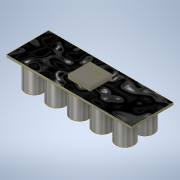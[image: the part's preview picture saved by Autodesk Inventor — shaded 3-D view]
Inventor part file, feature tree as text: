
AUTODESK INVENTOR PART (.ipt)
format: ipt  version: 2020 (Build 240168000, 168)  size: 611,840 bytes
history: native  units: mm
features: chamfer x16, extrude x10, sketch x10, other x2
ambient origin geometry x8: Origin, YZ Plane, XZ Plane, XY Plane, X Axis, Y Axis, Z Axis, Center Point
bodies: Body1 (feature_tree)
feature tree (38):
  other  "Bryła1"
  extrude  "Wyciągnięcie proste1"  Depth=10.0mm
  extrude  "Wyciągnięcie proste2"  Depth=55.88mm
  chamfer  "Faza1"  Distance=27.94mm
  chamfer  "Faza2"  Distance=1.0mm
  chamfer  "Faza3"  Distance=6.03mm
  extrude  "Wyciągnięcie proste3"  Depth=10.0mm
  chamfer  "Faza4"  Distance=2.54mm
  extrude  "Wyciągnięcie proste4"  Depth=10.0mm
  chamfer  "Faza5"  Distance=5.08mm
  chamfer  "Faza6"  Distance=6.03mm
  chamfer  "Faza7"  Distance=1.27mm
  chamfer  "Faza8"  Distance=0.64mm
  chamfer  "Faza9"  Distance=5.08mm
  chamfer  "Faza10"  Distance=0.64mm
  chamfer  "Faza11"  Distance=5.08mm
  chamfer  "Faza12"  Distance=0.64mm
  chamfer  "Faza13"  Distance=5.08mm
  chamfer  "Faza14"  Distance=0.64mm
  chamfer  "Faza15"  Distance=5.08mm
  chamfer  "Faza16"  Distance=5.08mm
  other  "Płaszczyzna konstrukcyjna1"
  extrude  "Wyciągnięcie proste5"  Depth=10.0mm
  extrude  "Wyciągnięcie proste6"  Depth=10.0mm
  extrude  "Wyciągnięcie proste7"  Depth=10.0mm
  extrude  "Wyciągnięcie proste8"  Depth=10.0mm
  extrude  "Wyciągnięcie proste9"  Depth=10.0mm
  extrude  "Extrusion10"  Depth=10.0mm
  sketch  "Szkic1"
  sketch  "Szkic2"
  sketch  "Szkic3"
  sketch  "Szkic4"
  sketch  "Szkic5"
  sketch  "Szkic6"
  sketch  "Szkic7"
  sketch  "Szkic8"
  sketch  "Szkic9"
  sketch  "Sketch10"  dims[d0=18.73mm d1=9.365mm d2=55.88mm d3=27.94mm d4=1.0mm d5=0.0mm d6=6.03mm d7=5.08mm d8=2.54mm d9=1.27mm d10=5.08mm d11=6.03mm d12=1.27mm d13=0.64mm d14=5.08mm d15=6.03mm d16=1.27mm d17=0.64mm d18=5.08mm d19=6.03mm d20=1.27mm d21=0.64mm d22=5.08mm d23=6.03mm d24=1.27mm d25=0.64mm d26=5.08mm d27=6.03mm d28=5.08mm d29=6.03mm d30=5.08mm d31=6.03mm d32=5.08mm d33=6.03mm d34=0.64mm d35=0.64mm d36=0.64mm d37=0.64mm d38=1.27mm d39=1.27mm d40=1.27mm d41=1.27mm d42=6.03mm d43=5.08mm d44=6.03mm d45=5.08mm d46=6.03mm d47=5.08mm d48=1.59mm d49=0.0mm d50=0.0mm d51=0.0mm d52=0.0mm d53=0.0mm d54=5.08mm d55=6.03mm d56=5.08mm d57=6.03mm d58=0.64mm d59=0.0mm d60=0.0mm d61=0.0mm d62=5.08mm d63=6.03mm d64=5.08mm d65=6.03mm d66=0.64mm d67=0.0mm d68=0.0mm d69=0.0mm d70=5.08mm d71=6.03mm d72=5.08mm d73=6.03mm d74=0.64mm d75=0.0mm d76=0.0mm d77=0.0mm d78=1.0mm d79=0.0mm d80=0.2mm d81=2.0mm d82=45.0deg d83=0.2mm d84=2.0mm d85=45.0deg d86=0.5mm d87=2.0mm d88=45.0deg d89=6.35mm d90=3.18mm d91=0.32mm d92=0.93mm d93=6.35mm d94=3.18mm d95=0.32mm d96=0.0mm d97=6.35mm d98=3.18mm d99=2.54mm d100=0.0mm d101=6.35mm d102=3.18mm d103=6.35mm d104=3.18mm d105=6.35mm d106=3.18mm d107=6.35mm d108=3.18mm d109=0.0mm d110=0.0mm d111=2.54mm d112=2.54mm d113=2.54mm d114=2.54mm d115=6.35mm d116=3.18mm d117=6.35mm d118=3.18mm d119=2.54mm d120=2.54mm d121=0.35mm d122=0.0mm d123=0.35mm d124=2.0mm d125=45.0deg d126=1.4mm d127=3.0mm d128=0.15mm d129=2.86mm d130=1.4mm d131=3.0mm d132=2.86mm d133=0.15mm d134=1.4mm d135=3.0mm d136=2.86mm d137=0.15mm d138=1.1mm d139=0.0mm d140=0.6mm d141=2.0mm d142=4.363323mm d143=0.6mm d144=2.0mm d145=4.363323mm d146=0.6mm d147=2.0mm d148=4.363323mm d149=0.6mm d150=2.0mm d151=4.363323mm d152=0.6mm d153=2.0mm d154=4.363323mm d155=0.6mm d156=2.0mm d157=4.363323mm d158=0.6mm d159=2.0mm d160=4.363323mm d161=0.6mm d162=2.0mm d163=4.363323mm d164=0.6mm d165=2.0mm d166=4.363323mm d167=0.6mm d168=2.0mm d169=4.363323mm d170=0.6mm d171=2.0mm d172=4.363323mm d173=0.6mm d174=2.0mm d175=4.363323mm d176=2.45mm d177=7.0mm d178=7.0mm d179=5.4mm d180=5.08mm d181=7.0mm d182=7.0mm d183=7.0mm d184=7.0mm d185=5.4mm d186=0.0mm d187=0.0mm d188=3.5mm d189=1.0mm d190=0.0mm d191=1.0mm d192=0.0mm d193=10.0mm d194=10.0mm d195=5.0mm d196=5.0mm d197=1.6mm d198=0.0mm d199=1.0mm d200=0.0mm d201=8.0mm d202=8.0mm d203=8.89mm d204=7.62mm d205=7.62mm d206=8.0mm d207=10.16mm d208=0.0mm d209=8.0mm d210=8.0mm d211=8.0mm d212=8.0mm d213=10.16mm d214=10.16mm d215=10.16mm d216=8.0mm d217=8.0mm d218=8.0mm d219=5.08mm d220=0.0mm d221=0.0mm d222=0.0mm d223=0.0mm d224=10.5mm d225=0.0mm d226=10.0mm d227=0.0mm]
